# Revit family: Bathtub_Traditional_Clayton_ABY789N_TOTO
name_source: partatom
category: Plumbing Fixtures
revit_build: Autodesk Revit Architecture 2013 (Build: 20130531_2115(x64)
units: mm (PartAtom-declared; Revit-internal decimal feet)

## types (1)
- ABY789N
    04 CSI = 22 41 19
    95 CSI = 15410
    Assembly Code = D2010510
    CAD Drawing URL = http://assets.totousa.com
    CW Connection = No
    CWFU = 0
    Color Availability = #01  Cotton, #12  Sedona Beige
    Default Elevation = 0"
    Depth = 66"
    Description = Soaker Bathtub
    Finish = Metal - TOTO - Chrome - Polished
    HW Connection = No
    HWFU = 0
    Height = 24 3/8"
    Manufacturer = TOTO USA, Inc.
    Manufacturer Fax = (770) 282-0002
    Model = ABY789N
    Series = Clayton
    Shipping Weight = 80.00 lb
    Spec Sheet URL = http://assets.totousa.com
    Style = Traditional
    Subcategory = Bathtubs
    Toto BIM Number = BM-00041
    URL = http://www.totousa.com
    Vent Connection = Yes
    WFU = 0
    Warranty = 1 Year Limited Warranty on acrylic tub; 1 Year Limited Warranty on components and parts
    Warranty URL = http://www.totousa.com
    Waste Connection = Yes
    Waste Connection NPT = 2"
    Waste Connection NPT Radius = 1"
    Width = 36"

## geometry (parser evidence)
native form markers: Blend x24, Sweep x4
no freeform markers — native parametric forms only
